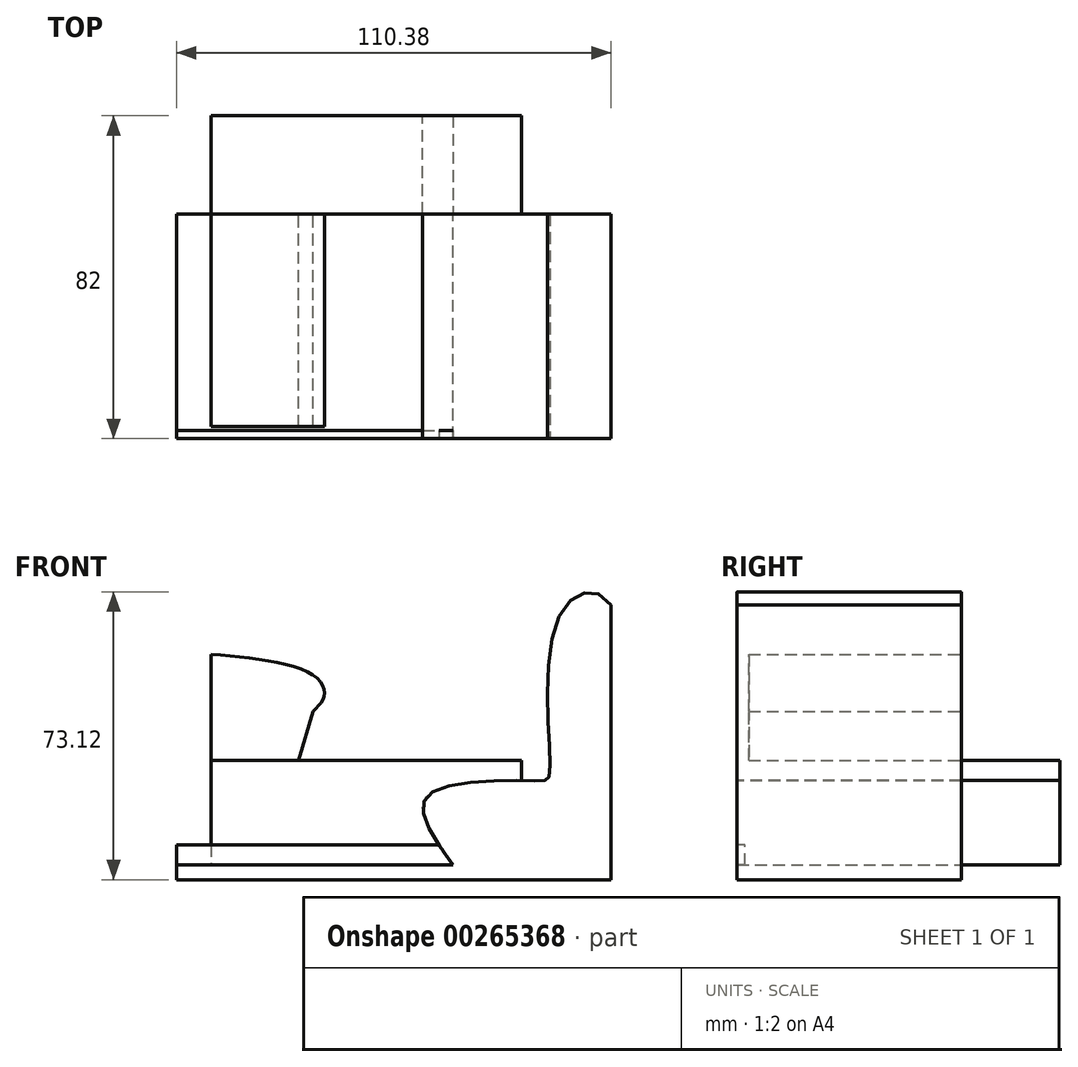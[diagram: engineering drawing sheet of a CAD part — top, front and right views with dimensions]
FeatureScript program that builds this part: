
annotation { "Feature Type Name" : "Feature", "Feature Type Description" : "" }
export const myFeature = defineFeature(function(context is Context, id is Id, definition is map)
    precondition{}
    {
        {
            var Q0;
            Q0=qCreatedBy(makeId("Front.planeOp"),FACE);
            var sketch = newSketch(context, id + "F0", { "sketchPlane" : qUnion([Q0])});
            skLineSegment(sketch, "E0.bottom", {"start": v(-52.37, -30.32) * mm, "end": v(58, -30.32) * mm});
            skLineSegment(sketch, "E0.top", {"start": v(-52.37, 75.93) * mm, "end": v(58, 75.93) * mm});
            skLineSegment(sketch, "E0.left", {"start": v(-52.37, -30.32) * mm, "end": v(-52.37, 75.93) * mm});
            skLineSegment(sketch, "E0.right", {"start": v(58, -30.32) * mm, "end": v(58, 75.93) * mm});
            skLineSegment(sketch, "E1", {"start": v(-52.37, -26.56) * mm, "end": v(17.83, -26.56) * mm});
            skFitSpline(sketch, "E2", {"points": [v(17.83, -26.56) * mm, v(11.64, -8.73) * mm, v(39.8, -5.16) * mm, v(42.43, -3.66) * mm, v(45.05, 37.08) * mm, v(58, 39.52) * mm, v(58, 9.86) * mm], "startDerivative": vector(-102.72, 146.21) * mm, "endDerivative": vector(-61.38, 44.33) * mm});
            skSolve(sketch);
        }
        {
            var Q0;
            {var subQ2=sQuery(id+"F0.wireOp",EDGE,"E0.bottom");Q0=makeQuery(id+"F0.imprint","IMPRINT",FACE,{"disambiguationData":[TD([[makeQuery(id+"F0.imprint","IMPRINT",EDGE,{"derivedFrom":subQ2}),1.0]])]});}
            extrude(context, id + "F1", {"entities" : qUnion([Q0]), "depth" : 57 * mm});
        }
        {
            var Q0;
            Q0=makeQuery(id+"F1.opExtrude","CAP_FACE",FACE,{"disambiguationData":[OSD([sQuery(id+"F0.wireOp",EDGE,"E0.bottom"),sQuery(id+"F0.wireOp",EDGE,"E0.left"),sQuery(id+"F0.wireOp",EDGE,"E0.right"),sQuery(id+"F0.wireOp",EDGE,"E1"),sQuery(id+"F0.wireOp",EDGE,"E2")])],"isStart":true});
            var sketch = newSketch(context, id + "F2", { "sketchPlane" : qUnion([Q0])});
            skLineSegment(sketch, "E3.bottom", {"start": v(-35.3, -30.32) * mm, "end": v(30.41, -30.32) * mm});
            skLineSegment(sketch, "E3.top", {"start": v(-35.3, 0) * mm, "end": v(21.37, 0) * mm});
            skLineSegment(sketch, "E3.left", {"start": v(-35.3, -30.32) * mm, "end": v(-35.3, 0) * mm});
            skLineSegment(sketch, "E4", {"start": v(21.37, 0) * mm, "end": v(17.65, 12.48) * mm});
            skFitSpline(sketch, "E5", {"points": [v(17.65, 12.48) * mm, v(14.83, 16.43) * mm, v(17.65, 21.68) * mm, v(43.55, 26.94) * mm, v(64.2, 27.5) * mm], "startDerivative": vector(-24.47, 23.82) * mm, "endDerivative": vector(59, 0.05) * mm});
            skLineSegment(sketch, "E6", {"start": v(43.55, 26.94) * mm, "end": v(43.55, -30.32) * mm});
            skLineSegment(sketch, "E7", {"start": v(43.55, -30.32) * mm, "end": v(30.41, -30.32) * mm});
            skPoint(sketch, "E3.right.end.orphan", {"position": v(30.41, 0) * mm});
            skLineSegment(sketch, "E8", {"start": v(21.37, 0) * mm, "end": v(43.55, 0) * mm});
            skSolve(sketch);
        }
        {
            var Q0;
            {var subQ7=sQuery(id+"F2.wireOp",EDGE,"E3.top");Q0=makeQuery(id+"F2.imprint","IMPRINT",FACE,{"disambiguationData":[TD([[makeQuery(id+"F2.imprint","IMPRINT",EDGE,{"derivedFrom":subQ7}),-1.0]])]});}
            extrude(context, id + "F3", {"entities" : qUnion([Q0]), "depth" : 25 * mm});
        }
        {
            var Q0;
            Q0=makeQuery(id+"F2.imprint","IMPRINT",FACE,{"disambiguationData":[TD([[makeQuery(id+"F2.imprint","IMPRINT",EDGE,{"derivedFrom":sQuery(id+"F2.wireOp",EDGE,"E4")}),-1.0]])]});
            extrude(context, id + "F4", {"entities" : qUnion([Q0]), "oppositeDirection" : true, "depth" : 54 * mm});
        }
        {
            var Q0;
            Q0=makeQuery(id+"F1.opExtrude","CAP_FACE",FACE,{"disambiguationData":[OSD([sQuery(id+"F0.wireOp",EDGE,"E0.bottom"),sQuery(id+"F0.wireOp",EDGE,"E0.left"),sQuery(id+"F0.wireOp",EDGE,"E0.right"),sQuery(id+"F0.wireOp",EDGE,"E1"),sQuery(id+"F0.wireOp",EDGE,"E2")])],"isStart":false});
            var sketch = newSketch(context, id + "F5", { "sketchPlane" : qUnion([Q0])});
            skLineSegment(sketch, "E9.bottom", {"start": v(-52.37, -30.32) * mm, "end": v(58, -30.32) * mm});
            skLineSegment(sketch, "E9.top", {"start": v(-52.37, -21.45) * mm, "end": v(58, -21.45) * mm});
            skLineSegment(sketch, "E9.left", {"start": v(-52.37, -30.32) * mm, "end": v(-52.37, -21.45) * mm});
            skLineSegment(sketch, "E9.right", {"start": v(58, -30.32) * mm, "end": v(58, -21.45) * mm});
            skSolve(sketch);
        }
        {
            var Q0;
            {var subQ5=makeQuery(id+"F1.opExtrude","CAP_EDGE",EDGE,{"disambiguationData":[OSD([sQuery(id+"F0.wireOp",EDGE,"E1")])],"isStart":false});Q0=makeQuery(id+"F5.imprint","IMPRINT",FACE,{"disambiguationData":[TD([[makeQuery(id+"F5.imprint","IMPRINT",EDGE,{"derivedFrom":subQ5}),1.0]])]});}
            extrude(context, id + "F6", {"entities" : qUnion([Q0]), "oppositeDirection" : true, "depth" : 2 * mm});
        }
    });
